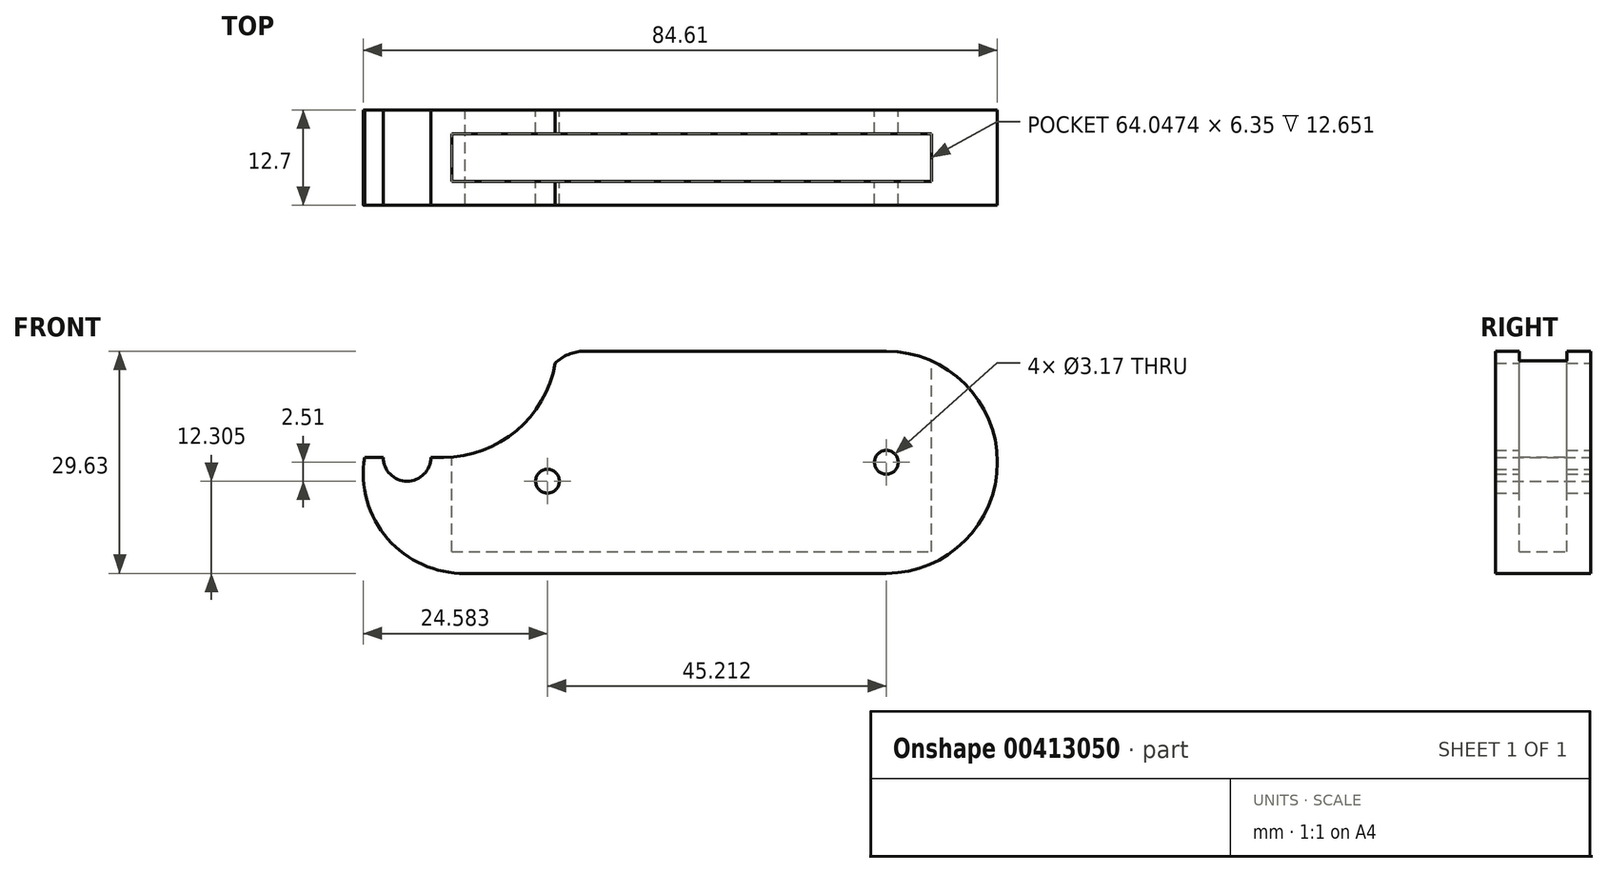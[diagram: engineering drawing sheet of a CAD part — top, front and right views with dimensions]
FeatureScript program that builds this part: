
annotation { "Feature Type Name" : "Feature", "Feature Type Description" : "" }
export const myFeature = defineFeature(function(context is Context, id is Id, definition is map)
    precondition{}
    {
        {
            var Q0;
            Q0=qCreatedBy(makeId("Front.planeOp"),FACE);
            var sketch = newSketch(context, id + "F0", { "sketchPlane" : qUnion([Q0])});
            skArc(sketch, "E0", {"start": v(-3.18, 0) * mm, "mid": v(0, -3.18) * mm, "end": v(3.18, 0) * mm});
            skLineSegment(sketch, "E1", {"start": v(3.18, 0) * mm, "end": v(4.87, 0) * mm});
            skArc(sketch, "E2", {"start": v(4.87, 0) * mm, "mid": v(14.6, 3.55) * mm, "end": v(19.76, 12.54) * mm});
            skLineSegment(sketch, "E3", {"start": v(23.62, 14.15) * mm, "end": v(63.95, 14.15) * mm});
            skArc(sketch, "E4", {"start": v(-5.68, 0) * mm, "mid": v(-2.58, -10.86) * mm, "end": v(7.74, -15.48) * mm});
            skLineSegment(sketch, "E5", {"start": v(7.74, -15.48) * mm, "end": v(63.95, -15.48) * mm});
            skArc(sketch, "E6", {"start": v(23.62, 14.15) * mm, "mid": v(21.53, 13.73) * mm, "end": v(19.76, 12.54) * mm});
            skArc(sketch, "E7", {"start": v(63.95, 14.15) * mm, "mid": v(78.76, -0.67) * mm, "end": v(63.95, -15.48) * mm});
            skCircle(sketch, "E8", {"center": v(63.95, -0.67) * mm, "radius": 1.59 * mm});
            skLineSegment(sketch, "E9", {"start": v(-5.68, 0) * mm, "end": v(-3.18, 0) * mm});
            skLineSegment(sketch, "E10", {"start": v(6.33, -3.18) * mm, "end": v(31.14, -3.18) * mm, "construction": true});
            skCircle(sketch, "E11", {"center": v(18.73, -3.18) * mm, "radius": 1.59 * mm});
            skSolve(sketch);
        }
        {
            var Q0;
            Q0 = qSketchRegion(id + "F0", true);
            extrude(context, id + "F1", {"entities" : qUnion([Q0]), "depth" : 6.35 * mm, "hasSecondDirection" : true, "secondDirectionOppositeDirection" : true, "secondDirectionDepth" : 6.35 * mm});
        }
        {
            var Q0;
            Q0=qCreatedBy(makeId("Front.planeOp"),FACE);
            var sketch = newSketch(context, id + "F2", { "sketchPlane" : qUnion([Q0])});
            skLineSegment(sketch, "E12.bottom", {"start": v(5.94, -12.61) * mm, "end": v(70, -12.61) * mm});
            skLineSegment(sketch, "E12.top", {"start": v(5.94, 20.71) * mm, "end": v(70, 20.71) * mm});
            skLineSegment(sketch, "E12.left", {"start": v(5.94, -12.61) * mm, "end": v(5.94, 20.71) * mm});
            skLineSegment(sketch, "E12.right", {"start": v(70, -12.61) * mm, "end": v(70, 20.71) * mm});
            skSolve(sketch);
        }
        {
            var Q0;
            Q0 = qSketchRegion(id + "F2", true);
            extrude(context, id + "F3", {"entities" : qUnion([Q0]), "operationType" : NewBodyOperationType.REMOVE, "depth" : 3.17 * mm, "hasSecondDirection" : true, "secondDirectionOppositeDirection" : true, "secondDirectionDepth" : 3.17 * mm});
        }
    });
